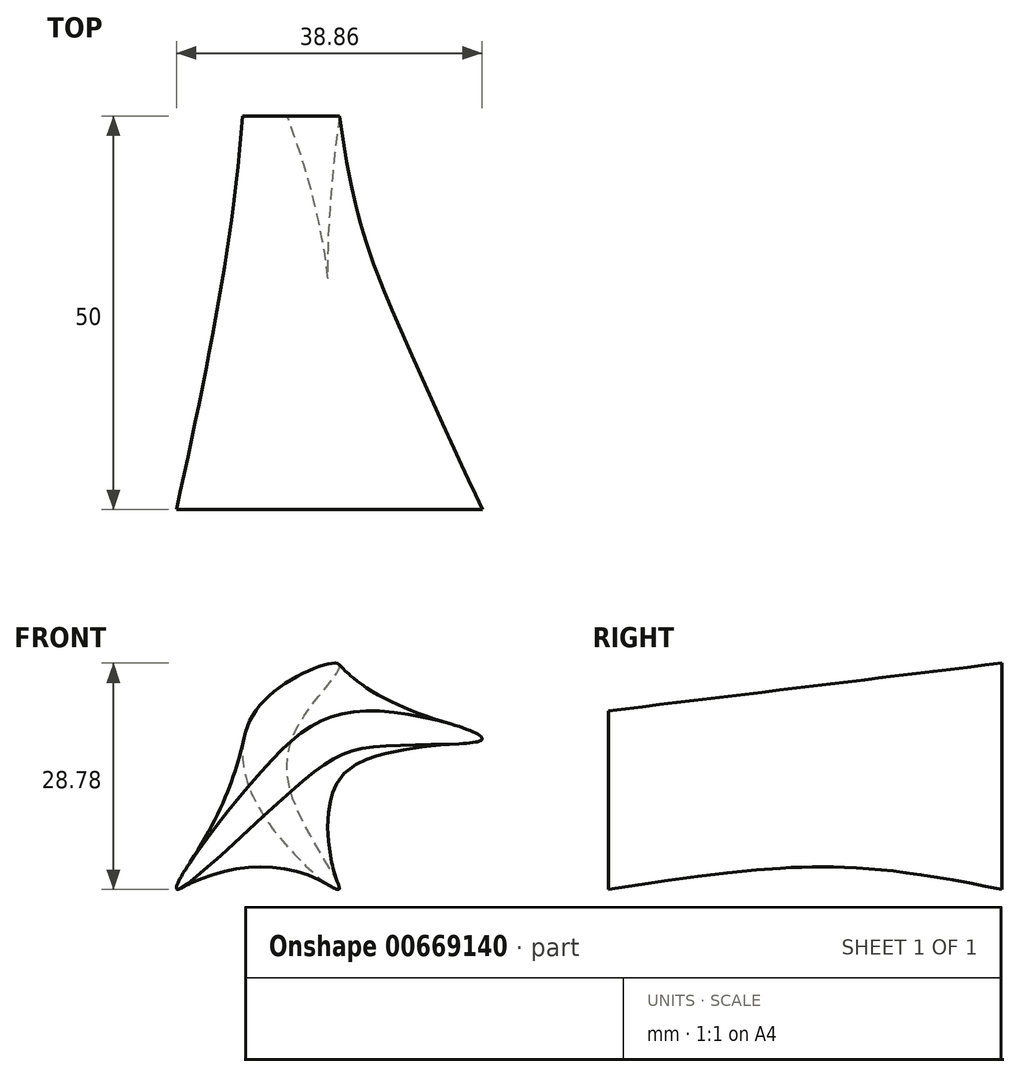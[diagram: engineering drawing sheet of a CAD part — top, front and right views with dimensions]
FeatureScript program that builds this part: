
annotation { "Feature Type Name" : "Feature", "Feature Type Description" : "" }
export const myFeature = defineFeature(function(context is Context, id is Id, definition is map)
    precondition{}
    {
        {
            var Q0;
            Q0=qCreatedBy(makeId("Front.planeOp"),FACE);
            var sketch = newSketch(context, id + "F0", { "sketchPlane" : qUnion([Q0])});
            skFitSpline(sketch, "E0", {"points": [v(0, 0) * mm, v(-5.48, 10.5) * mm, v(-4.59, 21.76) * mm, v(0, 28.57) * mm, v(-9.62, 23.83) * mm, v(-9.92, 9.92) * mm, v(0, 0) * mm]});
            skSolve(sketch);
        }
        {
            var Q0;
            Q0=qCreatedBy(makeId("Front.planeOp"),FACE);
            cPlane(context, id + "F1", {"entities" : qUnion([Q0]), "cplaneType" : CPlaneType.OFFSET, "offset" : 50 * mm, "width" : 150 * mm, "height" : 150 * mm});
        }
        {
            var Q0;
            Q0=qCreatedBy(id+"F1.planeOp",FACE);
            var sketch = newSketch(context, id + "F2", { "sketchPlane" : qUnion([Q0])});
            skFitSpline(sketch, "E1", {"points": [v(-20.58, 0) * mm, v(-4.88, 13.47) * mm, v(5.77, 18.2) * mm, v(18.2, 19.1) * mm, v(4.59, 22.65) * mm, v(-9.62, 15.25) * mm, v(-20.58, 0) * mm]});
            skSolve(sketch);
        }
        {
            var Q0;
            Q0 = qSketchRegion(id + "F2", true);
            var Q1;
            Q1 = qSketchRegion(id + "F0", true);
            loft(context, id + "F3", {"sheetProfilesArray" : [{ "sheetProfileEntities" : qUnion([Q0]) }, { "sheetProfileEntities" : qUnion([Q1]) }]});
        }
    });
